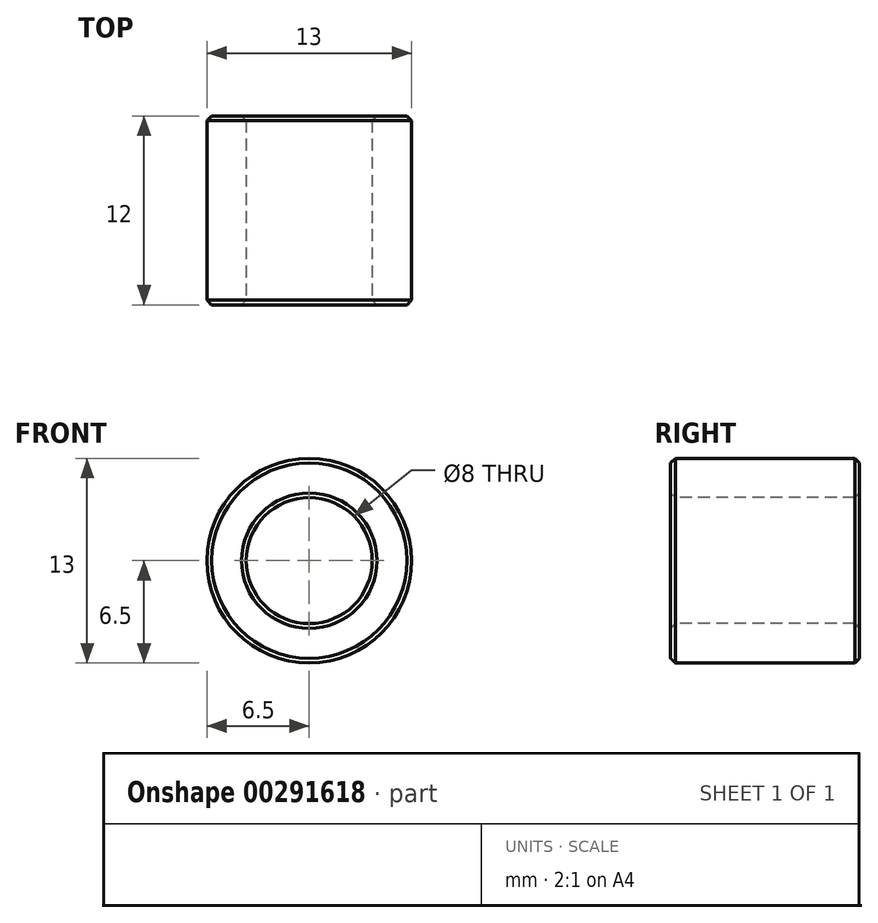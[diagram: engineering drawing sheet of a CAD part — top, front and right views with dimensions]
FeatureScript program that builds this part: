
annotation { "Feature Type Name" : "Feature", "Feature Type Description" : "" }
export const myFeature = defineFeature(function(context is Context, id is Id, definition is map)
    precondition{}
    {
        {
            var Q0;
            Q0=qCreatedBy(makeId("Front.planeOp"),FACE);
            var sketch = newSketch(context, id + "F0", { "sketchPlane" : qUnion([Q0])});
            skCircle(sketch, "E0", {"center": v(0, 0) * mm, "radius": 6.5 * mm});
            skCircle(sketch, "E1", {"center": v(0, 0) * mm, "radius": 4 * mm});
            skSolve(sketch);
        }
        {
            var Q0;
            Q0=makeQuery(id+"F0.imprint","IMPRINT",FACE,{"disambiguationData":[TD([[makeQuery(id+"F0.imprint","IMPRINT",EDGE,{"derivedFrom":sQuery(id+"F0.wireOp",EDGE,"E0")}),1.0]])]});
            var Q1;
            Q1=sQuery(id+"F0.wireOp",EDGE,"E0");
            extrude(context, id + "F1", {"entities" : qUnion([Q0]), "surfaceEntities" : qUnion([Q1]), "oppositeDirection" : true, "depth" : 12 * mm});
        }
        {
            var Q0;
            Q0=makeQuery(id+"F1.opExtrude","CAP_EDGE",EDGE,{"disambiguationData":[OSD([sQuery(id+"F0.wireOp",EDGE,"E0")])],"isStart":true});
            var Q1;
            Q1=makeQuery(id+"F1.opExtrude","CAP_EDGE",EDGE,{"disambiguationData":[OSD([sQuery(id+"F0.wireOp",EDGE,"E0")])],"isStart":false});
            var Q2;
            Q2=makeQuery(id+"F1.opExtrude","CAP_EDGE",EDGE,{"disambiguationData":[OSD([sQuery(id+"F0.wireOp",EDGE,"E1")])],"isStart":true});
            var Q3;
            Q3=makeQuery(id+"F1.opExtrude","CAP_EDGE",EDGE,{"disambiguationData":[OSD([sQuery(id+"F0.wireOp",EDGE,"E1")])],"isStart":false});
            chamfer(context, id + "F2", {"entities" : qUnion([Q0, Q1, Q2, Q3]), "width" : 0.3 * mm, "tangentPropagation" : true});
        }
    });
